# Revit family: Pendelaufhänger M10 und M12
name_source: partatom
category: HLS-Bauteile
revit_build: Autodesk Revit 2017 (Build: 20190507_1515(x64)
units: mm (PartAtom-declared; Revit-internal decimal feet)

## family parameters
Arbeitsebenenbasiert = Ja
Beim Laden mit Abzugskörper schneiden = Nein
Bemaßung runder Anschluss = Durchmesser verwenden
Gemeinsam genutzt = Ja
Immer vertikal = Nein
Raumberechnungspunkt = Nein
Teiletyp = Normal

## types (2) — shared parameters
B = 55 mm  [stored 0.180446 ft]
C = 15 mm  [stored 0.0492126 ft]
Fabrikat = MEFA
Firma = MEFA Befestigungs- und Montagesysteme GmbH
Gewindetyp = AG-AG
Höhe = 44 mm
Kurztext1 = Pendelaufhänger 15°
Material = Stahl
Mengeneinheit = St
Oberflaeche = galvanisch verzinkt
Pendelwinkel = 15
Vorgabe-Ansicht = 1219 mm
vpe = 50 St

## per-type parameters (varying)
| type | Artikelnummer | EAN | Gewicht | Gewicht pro Bauteil | Gewinde | Kurztext2 | L | Länge Gewinde | Mutter DIN928 | Pendelschraube | Sechskantmutter | max. zul. Last |
| Pendelaufhänger M10/M10 | 0784136 | 4250928418920 | 0.12 kg | 0.12 kg | M10-M10 | AG-AG M10-M10 | 22 mm  [stored 0.0721785 ft] | 22 mm  [stored 0.0721785 ft] | Mutter DIN 928 : Mutter DIN 928 M10 | Pendelschraube : Pendelschraube M10 | MEFA Sechskantmutter : Sechskantmutter M10 | 3.00 kN |
| Pendelaufhänger M12/M12 | 0784250 | 4250928418937 | 0.14 kg | 0.14 kg | M12-M12 | AG-AG M12-M12 | 19 mm  [stored 0.062336 ft] | 20 mm  [stored 0.0656168 ft] | Mutter DIN 928 : Mutter DIN 928 M12 | Pendelschraube : Pendelschraube M12 | MEFA Sechskantmutter : Sechskantmutter M12 | 3.60 kN |

note: [stored X ft] marks values corroborated as IEEE doubles in the binary element streams (Revit-internal decimal feet)

## geometry (parser evidence)
native form markers: Sweep x1
no freeform markers — native parametric forms only
